# Revit family: SYSCOOL FLOOR 60 HP R, внутренний блок
name_source: partatom
category: Оборудование
units: mm (PartAtom-declared; Revit-internal decimal feet)

## family parameters
Всегда вертикально = Да
Заголовок OmniClass = Climate Control (HVAC)
На основе рабочей плоскости = Нет
Номер OmniClass = 23.75.00.00
Общий = Нет
При загрузке вырезать с полостями = Нет
Размер круглого соединителя = Использовать диаметр
Тип детали = Нормальный
Точка расчета площади = Нет

## types (1)
- MFM-50ARN1-RB4WJ1
    Air  Flow = 2326/1984 m3/h
    Combine = 3900 Вт
    Combine Capacity = 3517 Вт
    Cooling Capacity = 17145 Вт
    Cooling Power Input = 6700 Вт
    Depth = 455 мм
    Gas = R410A
    Gas pipe = 19 мм
    Heating Capacity = 18904 Вт
    Heating Power Input = 5590 Вт
    Height = 1934 мм
    Installation = Indoor installation
    Liquid pipe = 9.52 мм
    Machine material = Galvanized Steel
    Net Weight = 67.00 кг
    Panel color = Polar white
    Power supply = 3 phase,380-415V, 50Hz
    Series = M
    Width = 600 мм
    clearance access behind = 50 мм
    clearance access front = 2000 мм
    clearance access left = 500 мм
    clearance access right = 500 мм
    clearance access up = 300 мм
    Группа модели = MFM-50ARN1-RB4WJ1
    Описание = Floor standing

## geometry (parser evidence)
native form markers: Sweep x3
no freeform markers — native parametric forms only
